# Revit family: Water_Heaters_HAJDU_HAJDU-STA-800C-1000C_
name_source: partatom
category: Mechanical Equipment
units: mm (PartAtom-declared; Revit-internal decimal feet)

## family parameters
Always vertical = Yes
Classification = None
Cut with Voids When Loaded = No
Maintain Annotation Orientation = No
OmniClass Number = 23.31.29.13
OmniClass Title = Hot Water Tank Heaters
Part Type = Normal
Room Calculation Point = No
Round Connector Dimension = Use Diameter
Shared = No
Work Plane-Based = Yes

## types (2) — shared parameters
Case Material = Hajdu - Felület - Fehér
Csatlakozó magassága "A" = 415 mm  [stored 1.36155 ft]
Csatlakozó magassága "E" = 120 mm  [stored 0.393701 ft]
Csatlakozó magassága "F" = 380 mm
Církulációs csonk = 31.75 mm
Default Elevation = 1219.2 mm  [stored 4 ft]
Description = A HAJDU multienergiás, nagy űrtartalmú szolár STA...C tartályok alsó és felső harmadában is található egy csőkígyó, ami indirekt módon felfűti a tartályban található használati melegvizet. Szolár rendszerbe köthető; Aktív anódos korrózió védelem.
Elektromos futopatron csatlakozás = 38.1 mm  [stored 0.125 ft]
Hocserélo csatlakozás = 31.75 mm
Homéro csonk = 12.7 mm  [stored 0.0416667 ft]
Korrózióvédelem = tűzzománc + aktív anód
Manufacturer = HAJDU
Product Page URL = https://hajdurt.hu
Rádiusz = 500 mm  [stored 1.64042 ft]
Tartály = tűzzománcozott acéllemez
URL = https://hajdurt.hu
Vízcsatlakozás = 38.1 mm  [stored 0.125 ft]
Átméro = 1000 mm  [stored 3.28084 ft]
Érzékelo tokcso = 12.7 mm  [stored 0.0416667 ft]
Üzemi nyomás = 0.6 MPa

## per-type parameters (varying)
| type | Csatlakozó magassága "B" | Csatlakozó magassága "C" | Csatlakozó magassága "G" | Csatlakozó magassága "I" | Csatlakozó magassága "J" | Csúcsteljesítmény | Hocserélo felulete | Hocserélo névleges urtartalma | Hocserélo tartós teljesítmény | Hocserélo áramlási ellenállása max. | Készenléti energia | Magasság | Névleges urtartalom | Tartos teljesítmény | Tömeg |
| STA 800C | 1080 mm  [stored 3.54331 ft] | 1125 mm | 860 mm | 1025 mm  [stored 3.36286 ft] | 1580 mm  [stored 5.18373 ft] | 1200 liter/az első 10 perc | 2 m2 | 14 l | 60 kW | 42 mbar | 2.66 kWh/24h | 2000 mm  [stored 6.56168 ft] | 800 l | 878 liter/h | 241.00 kg |
| STA 1000C | 1255 mm  [stored 4.11745 ft] | 1300 mm  [stored 4.26509 ft] | 1025 mm  [stored 3.36286 ft] | 1190 mm  [stored 3.9042 ft] | 1920 mm  [stored 6.29921 ft] | 1500 liter/az első 10 perc | 2.4 m2 | 16.8 l | 72 kW | 48 mbar | 3.09 kWh/24h | 2350 mm | 1000 l | 952 liter/h | 257.00 kg |

note: column(s) folded — value = type name in every type: Model

note: [stored X ft] marks values corroborated as IEEE doubles in the binary element streams (Revit-internal decimal feet)

## geometry (parser evidence)
native form markers: Sweep x5
no freeform markers — native parametric forms only
